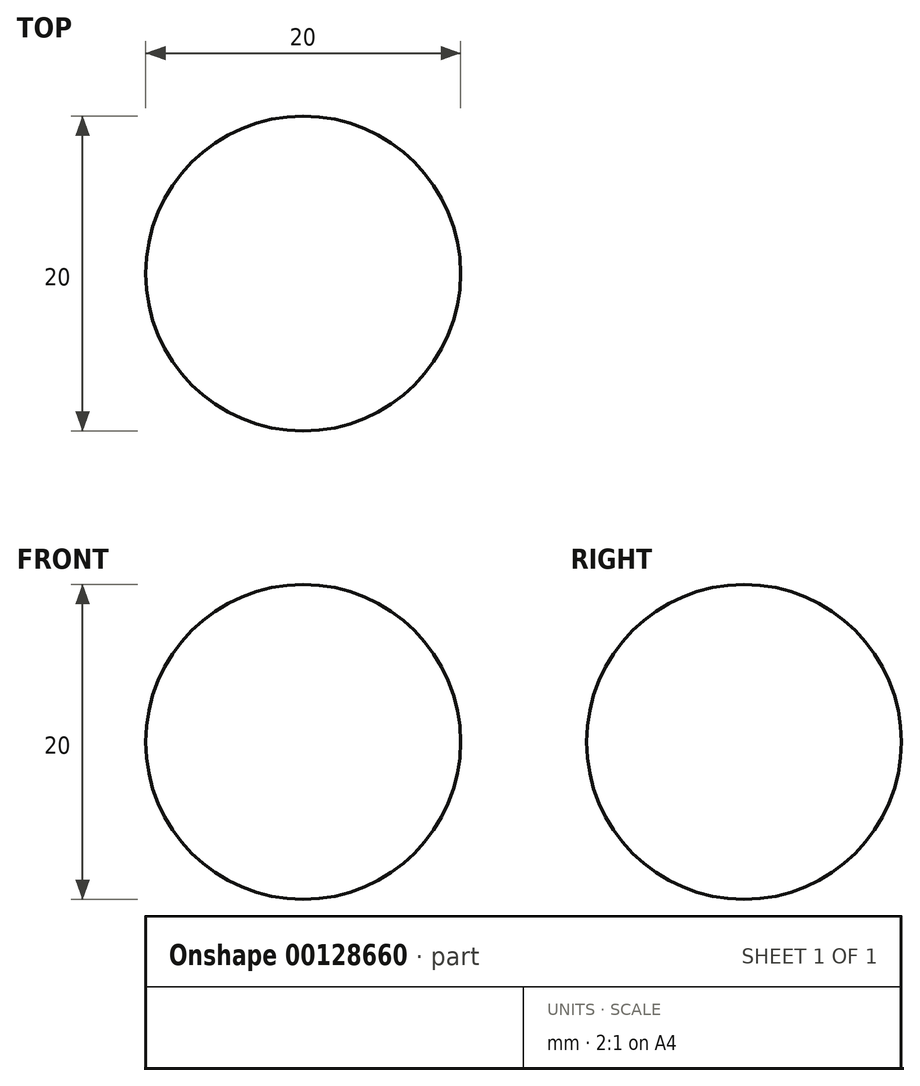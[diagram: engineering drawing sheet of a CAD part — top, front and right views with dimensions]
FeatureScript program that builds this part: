
annotation { "Feature Type Name" : "Feature", "Feature Type Description" : "" }
export const myFeature = defineFeature(function(context is Context, id is Id, definition is map)
    precondition{}
    {
        {
            var Q0;
            Q0=qCreatedBy(makeId("Front.planeOp"),FACE);
            var sketch = newSketch(context, id + "F0", { "sketchPlane" : qUnion([Q0])});
            skCircle(sketch, "E0", {"center": v(0, 0) * mm, "radius": 10 * mm});
            skLineSegment(sketch, "E1", {"start": v(0, 10) * mm, "end": v(0, -10) * mm});
            skSolve(sketch);
        }
        {
            var Q0;
            {var subQ0=sQuery(id+"F0.wireOp",EDGE,"E1");Q0=makeQuery(id+"F0.imprint","IMPRINT",FACE,{"disambiguationData":[TD([[makeQuery(id+"F0.imprint","IMPRINT",EDGE,{"derivedFrom":subQ0}),1.0]])]});}
            var Q1;
            Q1=sQuery(id+"F0.wireOp",EDGE,"E1");
            revolve(context, id + "F1", {"entities" : qUnion([Q0]), "axis" : qUnion([Q1]), "revolveType" : RevolveType.FULL});
        }
    });
